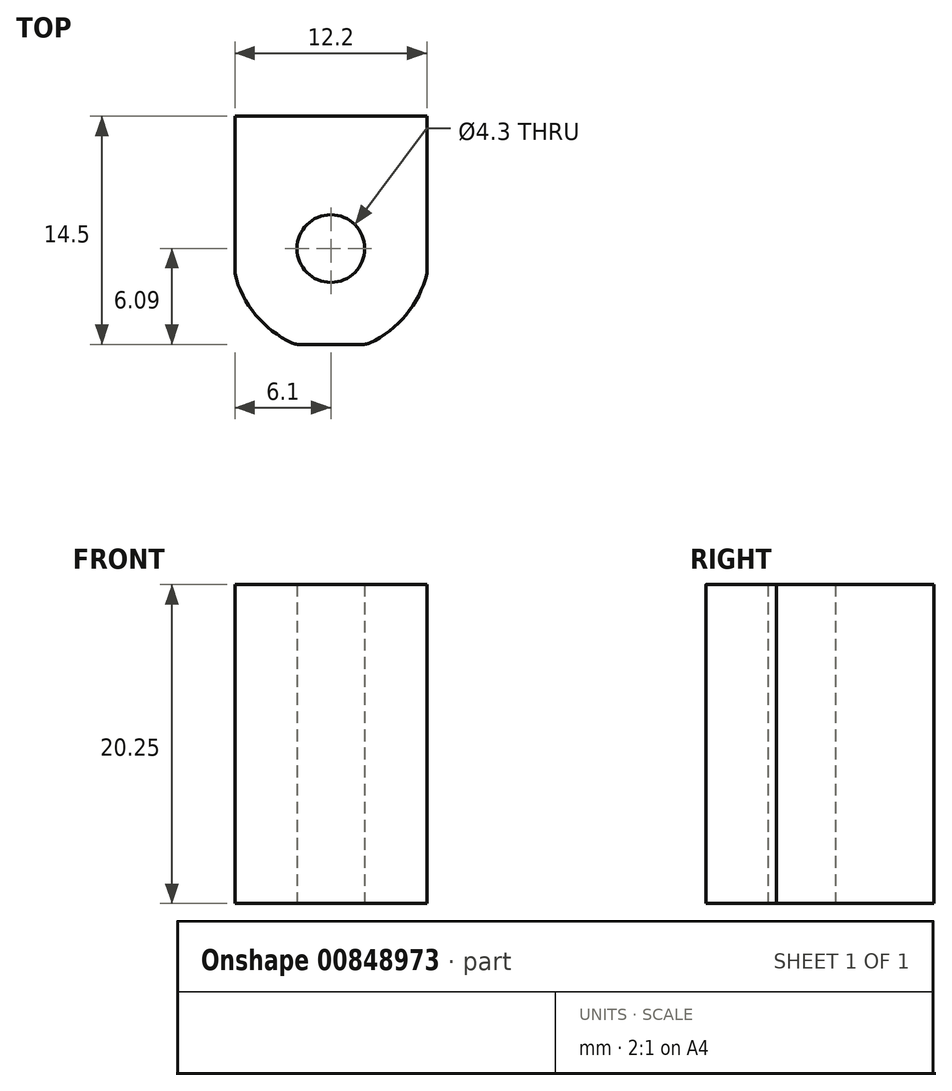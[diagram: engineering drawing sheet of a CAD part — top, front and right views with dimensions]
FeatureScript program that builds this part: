
annotation { "Feature Type Name" : "Feature", "Feature Type Description" : "" }
export const myFeature = defineFeature(function(context is Context, id is Id, definition is map)
    precondition{}
    {
        {
            var Q0;
            Q0=qCreatedBy(makeId("Top.planeOp"),FACE);
            var sketch = newSketch(context, id + "F0", { "sketchPlane" : qUnion([Q0])});
            skLineSegment(sketch, "E0.bottom", {"start": v(6.1, 8.41) * mm, "end": v(-6.1, 8.41) * mm});
            skLineSegment(sketch, "E0.left", {"start": v(6.1, 8.41) * mm, "end": v(6.1, -1.59) * mm});
            skLineSegment(sketch, "E0.right", {"start": v(-6.1, 8.41) * mm, "end": v(-6.1, -1.59) * mm});
            skArc(sketch, "E1", {"start": v(-6.1, -1.59) * mm, "mid": v(-4.7, -4.3) * mm, "end": v(-2.25, -6.09) * mm});
            skLineSegment(sketch, "E2", {"start": v(-2.25, -6.1) * mm, "end": v(0, -6.1) * mm});
            skArc(sketch, "E3.MirrorCS", {"start": v(6.1, -1.59) * mm, "mid": v(4.7, -4.3) * mm, "end": v(2.25, -6.09) * mm});
            skLineSegment(sketch, "E4.MirrorCS", {"start": v(2.25, -6.09) * mm, "end": v(0, -6.1) * mm});
            skCircle(sketch, "E5", {"center": v(0, 0) * mm, "radius": 2.15 * mm});
            skSolve(sketch);
        }
        {
            var Q0;
            Q0=makeQuery(id+"F0.imprint","IMPRINT",FACE,{"disambiguationData":[TD([[makeQuery(id+"F0.imprint","IMPRINT",EDGE,{"derivedFrom":sQuery(id+"F0.wireOp",EDGE,"E0.bottom")}),1.0]])]});
            extrude(context, id + "F1", {"entities" : qUnion([Q0]), "depth" : 20.25 * mm, "offsetDistance" : 25 * mm});
        }
        {
            var Q0;
            Q0=makeQuery(id+"F1.opExtrude","SWEPT_EDGE",EDGE,{"disambiguationData":[OSD([sQuery(id+"F0.wireOp",EDGE,"E1"),sQuery(id+"F0.wireOp",EDGE,"E2")])]});
            var Q1;
            Q1=makeQuery(id+"F1.opExtrude","SWEPT_EDGE",EDGE,{"disambiguationData":[OSD([sQuery(id+"F0.wireOp",EDGE,"E3.MirrorCS"),sQuery(id+"F0.wireOp",EDGE,"E4.MirrorCS")])]});
            fillet(context, id + "F2", {"entities" : qUnion([Q0, Q1]), "radius" : 1 * mm, "tangentPropagation" : true, "allowEdgeOverflow" : false});
        }
    });
